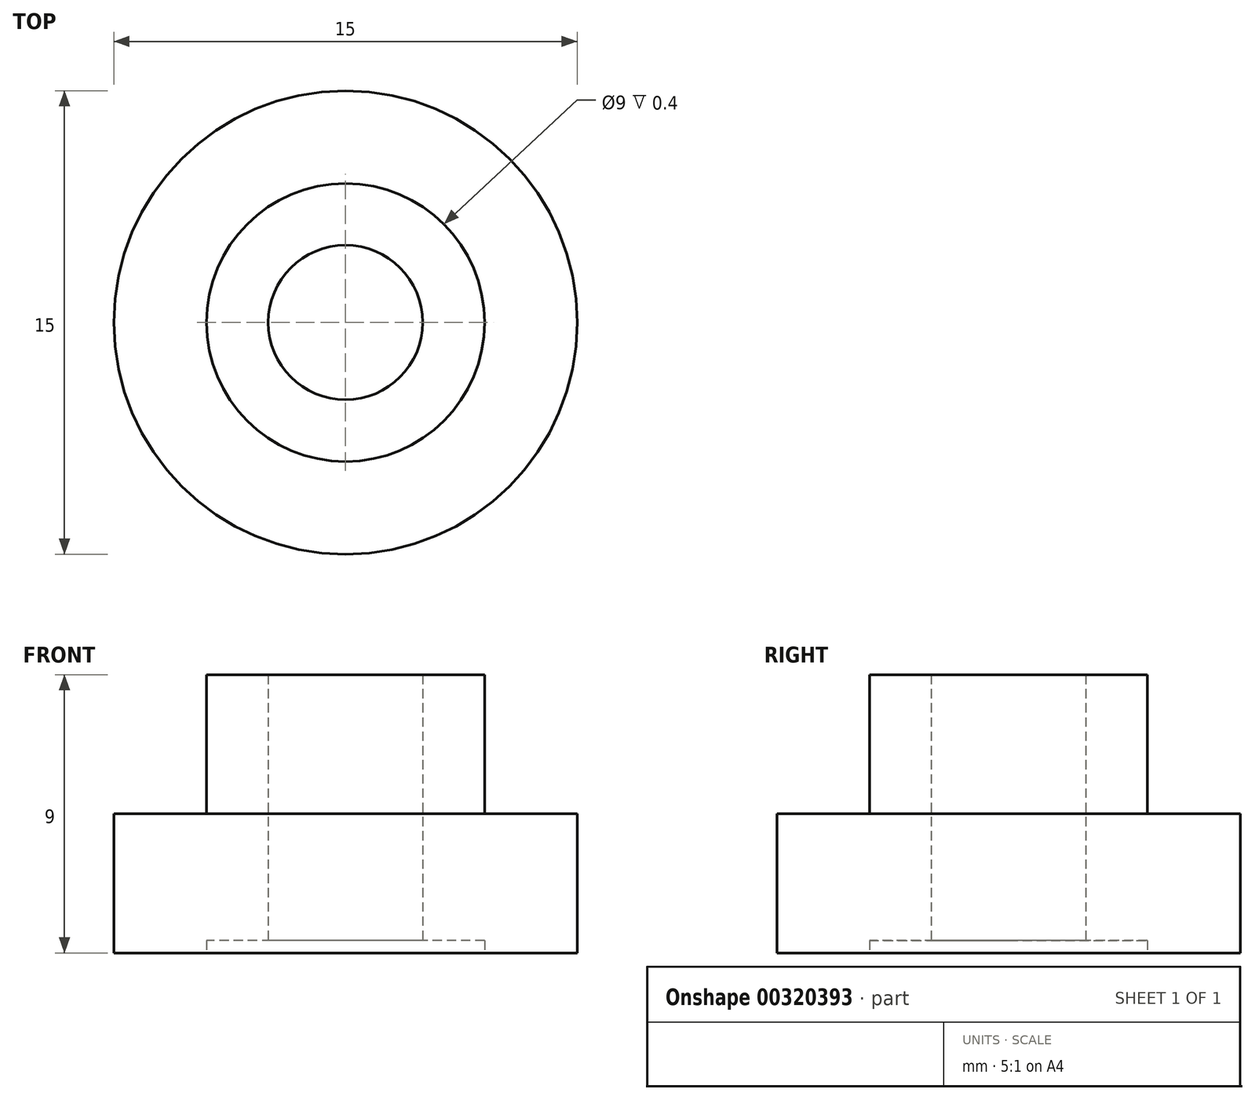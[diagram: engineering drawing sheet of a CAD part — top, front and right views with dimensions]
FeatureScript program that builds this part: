
annotation { "Feature Type Name" : "Feature", "Feature Type Description" : "" }
export const myFeature = defineFeature(function(context is Context, id is Id, definition is map)
    precondition{}
    {
        {
            var Q0;
            Q0=qCreatedBy(makeId("Top.planeOp"),FACE);
            var sketch = newSketch(context, id + "F0", { "sketchPlane" : qUnion([Q0])});
            skCircle(sketch, "E0", {"center": v(0, 0) * mm, "radius": 7.5 * mm});
            skCircle(sketch, "E1", {"center": v(0, 0) * mm, "radius": 4.5 * mm});
            skCircle(sketch, "E2", {"center": v(0, 0) * mm, "radius": 2.5 * mm});
            skSolve(sketch);
        }
        {
            var Q0;
            Q0=makeQuery(id+"F0.imprint","IMPRINT",FACE,{"disambiguationData":[TD([[makeQuery(id+"F0.imprint","IMPRINT",EDGE,{"derivedFrom":sQuery(id+"F0.wireOp",EDGE,"E1")}),1.0]])]});
            extrude(context, id + "F1", {"entities" : qUnion([Q0]), "depth" : 9 * mm});
        }
        {
            var Q0;
            Q0=makeQuery(id+"F0.imprint","IMPRINT",FACE,{"disambiguationData":[TD([[makeQuery(id+"F0.imprint","IMPRINT",EDGE,{"derivedFrom":sQuery(id+"F0.wireOp",EDGE,"E0")}),1.0]])]});
            var Q1;
            Q1=sQuery(id+"F0.wireOp",EDGE,"E0");
            extrude(context, id + "F2", {"entities" : qUnion([Q0]), "operationType" : NewBodyOperationType.ADD, "surfaceEntities" : qUnion([Q1]), "depth" : 4.5 * mm});
        }
        {
            var Q0;
            Q0=makeQuery(id+"F0.imprint","IMPRINT",FACE,{"disambiguationData":[TD([[makeQuery(id+"F0.imprint","IMPRINT",EDGE,{"derivedFrom":sQuery(id+"F0.wireOp",EDGE,"E1")}),1.0]])]});
            extrude(context, id + "F3", {"entities" : qUnion([Q0]), "operationType" : NewBodyOperationType.REMOVE, "depth" : 0.4 * mm});
        }
    });
